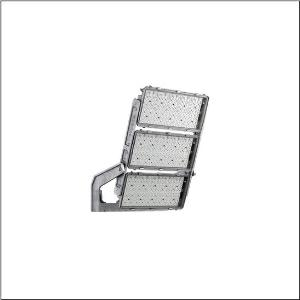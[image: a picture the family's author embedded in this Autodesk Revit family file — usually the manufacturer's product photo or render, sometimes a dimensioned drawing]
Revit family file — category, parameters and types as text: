
# Revit family: floodlight_fl_11_maxi_pro_remote___pl43_5xa779524a01aa_32ee
name_source: partatom
category: Lighting Fixtures
units: mm (PartAtom-declared; Revit-internal decimal feet)

## family parameters
Cut with Voids When Loaded = No
Host = Face
Light Source = No
Part Type = Normal
Room Calculation Point = No
Round Connector Dimension = Use Diameter
Shared = No

## types (1)
- --- (1 x LED, 130000 lm, 1334.7 W, 5700K)
    Apparent Load = 1335 VA
    CIE Flux Codes = 25 74 99 100 100
    Color Rendering = 90
    Color Temperature = 5700K
    Default Elevation = 1800 mm
    Description = Floodlight FL 11  maxi  pro Remote floodlight; light control with lens of PMMA; cover panel of toughened safety glass, transparent; light distribution: PL43, asymmetric direct distribution, LEDcolour temperature: 5700K, rated luminous flux: 130.000lm, colour rendering: CRI > 90, light colour: 957; luminous efficacy: 97lm/W; brightness control: DMX+RDM; with terminal, 8-pole, max. 2.5mm², mains connection: 220..240V/380..400V AC, 50/60Hz, surge voltage resistance: line to ground: 10kV, ECG replaceable separately, no afterglow with DALI off / DMX off command, LED unit replaceable without ESD environment, dustproof LED module, dimming range 10..100%; 1335W floodlight with 3x LED unit of diecast aluminium, coated grey; length: 713mm / width: 651mm / height: 338mm; mounting bracket, of diecast aluminium, uncoated, natural, equipment: Power, protection rating (complete): IP66; insulation class (complete): insulation class I (protective earthing); certification: CE, ENEC, VDE; ball protection: ball impact resistance with accessories, impact resistance: IK07; only for outdoor installations, rated ambient temperature 10°C, permissible operating ambient temperature: -40..+30°C, permissible storage temperature: -40..+85°C; packaging unit: 1 piece

Light Distribution: PL43
    Height = 320 mm
    Lamp = 1 x LED
    Lamp Light Flux = 130000 lm
    Lamp Power = 1334.7 W
    Lamp count = 1
    Length = 1002 mm
    Luminous efficacy = 97 lm/W
    Manufacturer = Siteco
    ModVariant = No
    Model = 5XA779524A01AA
    Mounting Place = Ceiling
    Mounting Type = Surface mounted
    Number of Poles = 1
    OnlyDefault = Yes
    Power Factor = 1
    Product Name = Floodlight FL 11 maxi pro Remote | PL43
    Product group = floodlight | ceiling mounted
    ProductGroupID = 302
    Protection Class = Protection class I
    Protection Degree = IP 66
    RLX_Detail_Level = 1
    RLX_Emergency_Light_Flux = 0 lm
    RLX_Emergency_Type = 0
    RLX_Emergency_Type_DB = No
    RlxData = <blob elided: 52425 chars, md5=ff4442cd>
    Socket = socket
    Standby Power = 0 W
    System Light Flux = 130000 lm
    System Power = 1335 W
    Type Comments = factory setting: luminous flux: 100 % | dim-lin: 255 | 920 mA
    Type Image = l_1006784.jpg
    URL = http://relux.com
    VarID = @adj_027057
    Voltage = 0 V
    Weight = 0.00 kg
    Width = 655 mm

## geometry (parser evidence)
native form markers: Blend x4, Sweep x14
no freeform markers — native parametric forms only
